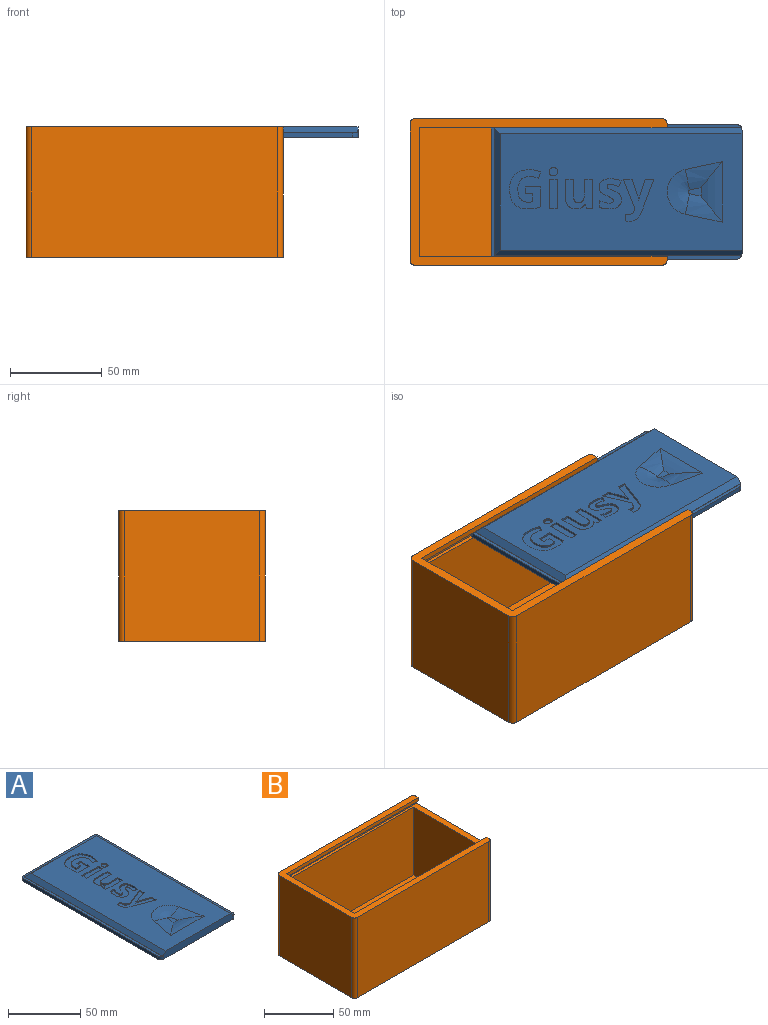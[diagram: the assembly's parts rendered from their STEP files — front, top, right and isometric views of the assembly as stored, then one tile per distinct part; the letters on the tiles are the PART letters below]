
ASSEMBLY  parts=2 mates=1
PART A: 116 faces, bbox 77.1x136.6x5.8 mm
  f0: plane 131.82x63.72mm, normal (0,0,1), area 6894.2mm2, adj f4,f10,f11,f12,f14,f15,f16,f17
  f1: plane 132.3x2.6mm, normal (1,0,0), area 344mm2, adj f5,f6,f112,f114
  f2: plane 70.7x2.6mm, normal (0,1,0), area 183.8mm2, adj f5,f6,f112,f113
  f3: plane 132.3x2.6mm, normal (-1,0,0), area 344mm2, adj f5,f6,f113,f115
  f4: plane 67.3x5.8mm, normal (0,-1,0), area 387.1mm2, adj f0,f6,f10,f11,f114,f115
  f5: plane 136.35x73.3mm, normal (0,0,1), area 612.8mm2, adj f1,f2,f3,f7,f8,f9,f112,f113
  f6: plane 136.6x73.3mm, normal (0,0,-1), area 10008.2mm2, adj f1,f2,f3,f4,f112,f113,f114,f115
  f7: plane 69.7x0.2mm, normal (0,1,0), area 13.9mm2, adj f5,f8,f9,f12
  f8: plane 134.55x0.2mm, normal (1,0,0), area 26.9mm2, adj f5,f7,f10,f114
  f9: plane 134.55x0.2mm, normal (-1,0,0), area 26.9mm2, adj f5,f7,f11,f115
  f10: plane 134.83x3.03mm, normal (0.71,0,0.71), area 565.4mm2, adj f0,f4,f8,f12,f114
  f11: plane 134.83x3.03mm, normal (-0.71,0,0.71), area 565.4mm2, adj f0,f4,f9,f12,f115
  f12: plane 69.7x3mm, normal (0,0.71,0.71), area 283mm2, adj f0,f7,f10,f11
  f13: plane 7.01x4.6mm, normal (0,0,1), area 21.5mm2, adj f14,f15,f16,f17
  f14: bspline ~22.47x15.51mm, area 157.5mm2, adj f0,f13,f15,f16
  f15: bspline ~24.43x12.28mm, area 213.3mm2, adj f0,f13,f14,f17
  f16: bspline ~57.85x11.49mm, area 220.1mm2, adj f0,f13,f14,f17
  f17: bspline ~22.47x15.51mm, area 157.5mm2, adj f0,f13,f15,f16
  f18: plane 15.81x6.33mm, normal (0.37,-0.93,0), area 17mm2, adj f0,f19,f34,f35
  f19: plane 1x0.78mm, normal (-0.31,-0.95,0), area 0.8mm2, adj f0,f18,f20,f35
  f20: extruded ~2.13x1.34mm, area 2.6mm2, adj f0,f19,f21,f35
  f21: extruded ~2.01x1mm, area 2.2mm2, adj f0,f20,f22,f35
  f22: extruded ~1.71x1mm, area 1.7mm2, adj f0,f21,f23,f35
  f23: plane 3.45x1mm, normal (0,-1,0), area 3.4mm2, adj f0,f22,f24,f35
  f24: extruded ~2.21x1mm, area 2.2mm2, adj f0,f23,f25,f35
  f25: extruded ~4.01x1.24mm, area 4.3mm2, adj f0,f24,f26,f35
  f26: extruded ~3.73x2.65mm, area 4.6mm2, adj f0,f25,f27,f35
  f27: plane 17.96x6.74mm, normal (0.35,0.94,0), area 19.2mm2, adj f0,f26,f28,f35
  f28: plane 4.66x1mm, normal (-1,0,0), area 4.7mm2, adj f0,f27,f29,f35
  f29: plane 8.96x2.95mm, normal (-0.31,-0.95,0), area 9.4mm2, adj f0,f28,f30,f35
  f30: extruded ~2.76x1mm, area 2.8mm2, adj f0,f29,f31,f35
  f31: plane 1x0.09mm, normal (-1,0,0), area 0.1mm2, adj f0,f30,f32,f35
  f32: extruded ~2.76x1mm, area 2.8mm2, adj f0,f31,f33,f35
  f33: plane 8.96x3mm, normal (-0.32,0.95,0), area 9.4mm2, adj f0,f32,f34,f35
  f34: plane 4.76x1mm, normal (-1,0,0), area 4.8mm2, adj f0,f18,f33,f35
  f35: plane 22.93x16.59mm, normal (0,0,1), area 165.6mm2, adj f18,f19,f20,f21,f22,f23,f24,f25
  f36: extruded ~2.04x1mm, area 2.1mm2, adj f0,f37,f61,f62
  f37: extruded ~1.51x1.28mm, area 2mm2, adj f0,f36,f38,f62
  f38: extruded ~2.73x1.41mm, area 3.1mm2, adj f0,f37,f39,f62
  f39: extruded ~2.72x1.27mm, area 3mm2, adj f0,f38,f40,f62
  f40: extruded ~1.01x1mm, area 1.2mm2, adj f0,f39,f41,f62
  f41: extruded ~1.92x1.04mm, area 2.4mm2, adj f0,f40,f42,f62
  f42: extruded ~2.12x1mm, area 2.2mm2, adj f0,f41,f43,f62
  f43: extruded ~2.24x1mm, area 2.4mm2, adj f0,f42,f44,f62
  f44: plane 3.13x1.31mm, normal (0.39,0.92,0), area 3.4mm2, adj f0,f43,f45,f62
  f45: extruded ~5.6x1.25mm, area 5.8mm2, adj f0,f44,f46,f62
  f46: extruded ~4.66x1.16mm, area 4.9mm2, adj f0,f45,f47,f62
  f47: extruded ~3.28x1.64mm, area 3.8mm2, adj f0,f46,f48,f62
  f48: extruded ~2.08x1mm, area 2.1mm2, adj f0,f47,f49,f62
  f49: extruded ~1.5x1.25mm, area 2mm2, adj f0,f48,f50,f62
  f50: extruded ~2.7x1.43mm, area 3.1mm2, adj f0,f49,f51,f62
  f51: extruded ~2.05x1mm, area 2.3mm2, adj f0,f50,f52,f62
  f52: extruded ~1.08x1mm, area 1.3mm2, adj f0,f51,f53,f62
  f53: extruded ~1x0.84mm, area 0.9mm2, adj f0,f52,f54,f62
  f54: extruded ~2.37x1.37mm, area 3.1mm2, adj f0,f53,f55,f62
  f55: extruded ~2.67x1mm, area 2.7mm2, adj f0,f54,f56,f62
  f56: extruded ~2.73x1mm, area 2.9mm2, adj f0,f55,f57,f62
  f57: plane 3.59x1mm, normal (0,-1,0), area 3.6mm2, adj f0,f56,f58,f62
  f58: extruded ~2.29x1mm, area 2.4mm2, adj f0,f57,f59,f62
  f59: extruded ~2.96x1mm, area 3mm2, adj f0,f58,f60,f62
  f60: extruded ~5.09x1.28mm, area 5.3mm2, adj f0,f59,f61,f62
  f61: extruded ~3.73x1.7mm, area 4.3mm2, adj f0,f36,f60,f62
  f62: plane 16.51x12.08mm, normal (0,0,1), area 127mm2, adj f36,f37,f38,f39,f40,f41,f42,f43
  f63: plane 3.33x1mm, normal (1,0,0), area 3.3mm2, adj f0,f64,f79,f80
  f64: plane 15.92x1mm, normal (0,1,0), area 15.9mm2, adj f0,f63,f65,f80
  f65: plane 4.34x1mm, normal (-1,0,0), area 4.3mm2, adj f0,f64,f66,f80
  f66: plane 7.49x1mm, normal (0,-1,0), area 7.5mm2, adj f0,f65,f67,f80
  f67: extruded ~4.04x1mm, area 4.2mm2, adj f0,f66,f68,f80
  f68: extruded ~2.63x1.22mm, area 3mm2, adj f0,f67,f69,f80
  f69: extruded ~1.95x1mm, area 2.2mm2, adj f0,f68,f70,f80
  f70: extruded ~2.58x1mm, area 2.7mm2, adj f0,f69,f71,f80
  f71: plane 9.3x1mm, normal (0,1,0), area 9.3mm2, adj f0,f70,f72,f80
  f72: plane 4.34x1mm, normal (-1,0,0), area 4.3mm2, adj f0,f71,f73,f80
  f73: plane 10.38x1mm, normal (0,-1,0), area 10.4mm2, adj f0,f72,f74,f80
  f74: extruded ~4.33x1.42mm, area 4.7mm2, adj f0,f73,f75,f80
  f75: extruded ~4.23x1.5mm, area 4.6mm2, adj f0,f74,f76,f80
  f76: extruded ~2.92x1mm, area 3mm2, adj f0,f75,f77,f80
  f77: extruded ~1.98x1.72mm, area 2.7mm2, adj f0,f76,f78,f80
  f78: plane 1x0.23mm, normal (1,0,0), area 0.2mm2, adj f0,f77,f79,f80
  f79: plane 2.04x1mm, normal (0.28,-0.96,0), area 2.1mm2, adj f0,f63,f78,f80
  f80: plane 16.21x14.7mm, normal (0,0,1), area 154.7mm2, adj f63,f64,f65,f66,f67,f68,f69,f70
  f81: plane 15.92x1mm, normal (0,1,0), area 15.9mm2, adj f0,f82,f84,f85
  f82: plane 4.34x1mm, normal (-1,0,0), area 4.3mm2, adj f0,f81,f83,f85
  f83: plane 15.92x1mm, normal (0,-1,0), area 15.9mm2, adj f0,f82,f84,f85
  f84: plane 4.34x1mm, normal (1,0,0), area 4.3mm2, adj f0,f81,f83,f85
  f85: plane 15.92x4.34mm, normal (0,0,1), area 69.2mm2, adj f81,f82,f83,f84
  f86: extruded ~2.37x2.14mm, area 3.7mm2, adj f0,f87,f90,f91
  f87: extruded ~1.78x1mm, area 1.9mm2, adj f0,f86,f88,f91
  f88: extruded ~1.57x1mm, area 1.7mm2, adj f0,f87,f89,f91
  f89: extruded ~2.37x2.12mm, area 3.6mm2, adj f0,f88,f90,f91
  f90: extruded ~2.37x2.12mm, area 3.6mm2, adj f0,f86,f89,f91
  f91: plane 4.73x4.26mm, normal (0,0,1), area 16.8mm2, adj f86,f87,f88,f89,f90
  f92: plane 3.68x1mm, normal (0,-1,0), area 3.7mm2, adj f0,f93,f110,f111
  f93: plane 3.95x1mm, normal (1,0,0), area 3.9mm2, adj f0,f92,f94,f111
  f94: plane 4.34x1mm, normal (0,-1,0), area 4.3mm2, adj f0,f93,f95,f111
  f95: extruded ~2.81x1mm, area 2.8mm2, adj f0,f94,f96,f111
  f96: extruded ~4.04x1.79mm, area 4.6mm2, adj f0,f95,f97,f111
  f97: extruded ~5.18x1.39mm, area 5.5mm2, adj f0,f96,f98,f111
  f98: extruded ~5.17x1.72mm, area 5.6mm2, adj f0,f97,f99,f111
  f99: extruded ~4.58x1.92mm, area 5.1mm2, adj f0,f98,f100,f111
  f100: extruded ~4.74x1.14mm, area 4.9mm2, adj f0,f99,f101,f111
  f101: plane 3.53x1.47mm, normal (0.38,0.92,0), area 3.8mm2, adj f0,f100,f102,f111
  f102: extruded ~6.18x1.28mm, area 6.4mm2, adj f0,f101,f103,f111
  f103: extruded ~7.99x2.82mm, area 8.7mm2, adj f0,f102,f104,f111
  f104: extruded ~7.86x2.88mm, area 8.6mm2, adj f0,f103,f105,f111
  f105: extruded ~7.96x2.49mm, area 8.5mm2, adj f0,f104,f106,f111
  f106: extruded ~7.2x2.77mm, area 8mm2, adj f0,f105,f107,f111
  f107: extruded ~3.62x1mm, area 3.6mm2, adj f0,f106,f108,f111
  f108: extruded ~3.78x1mm, area 3.9mm2, adj f0,f107,f109,f111
  f109: plane 10.8x1mm, normal (0,1,0), area 10.8mm2, adj f0,f108,f110,f111
  f110: plane 8.26x1mm, normal (-1,0,0), area 8.3mm2, adj f0,f92,f109,f111
  f111: plane 21.41x17.09mm, normal (0,0,1), area 211.2mm2, adj f92,f93,f94,f95,f96,f97,f98,f99
  f112: cylinder r=1.3mm len=2.6mm, axis (0,0,1), area 5.3mm2, adj f1,f2,f5,f6
  f113: cylinder r=1.3mm len=2.6mm, axis (0,0,-1), area 5.3mm2, adj f2,f3,f5,f6
  f114: cylinder r=3mm len=4mm, axis (0,0,-1), area 13.2mm2, adj f1,f4,f5,f6,f8,f10
  f115: cylinder r=3mm len=4mm, axis (0,0,1), area 13.2mm2, adj f3,f4,f5,f6,f9,f11
PART B: 27 faces, bbox 140x80x71 mm
  f0: plane 74x65mm, normal (1,0,0), area 4810mm2, adj f13,f15,f20,f23
  f1: plane 3x2mm, normal (1,0,0), area 6mm2, adj f2,f16,f23,f26
  f2: plane 135x3mm, normal (0,1,0), area 405mm2, adj f1,f3,f16,f26
  f3: plane 70x3mm, normal (1,0,0), area 210mm2, adj f2,f9,f16,f26
  f4: plane 130x60mm, normal (0,-1,0), area 7800mm2, adj f5,f11,f14,f15
  f5: plane 70x60mm, normal (-1,0,0), area 4200mm2, adj f4,f10,f14,f15
  f6: plane 3x2mm, normal (1,0,0), area 6mm2, adj f9,f16,f20,f26
  f7: plane 134x71mm, normal (0,1,0), area 9514mm2, adj f13,f20,f21,f26
  f8: plane 74x71mm, normal (-1,0,0), area 5254mm2, adj f13,f21,f22,f26
  f9: plane 135x3mm, normal (0,-1,0), area 405mm2, adj f3,f6,f16,f26
  f10: plane 130x60mm, normal (0,1,0), area 7800mm2, adj f5,f11,f14,f15
  f11: plane 70x60mm, normal (1,0,0), area 4200mm2, adj f4,f10,f14,f15
  f12: plane 134x71mm, normal (0,-1,0), area 9514mm2, adj f13,f22,f23,f26
  f13: plane 140x80mm, normal (0,0,-1), area 11192.3mm2, adj f0,f7,f8,f12,f20,f21,f22,f23
  f14: plane 130x70mm, normal (0,0,1), area 9100mm2, adj f4,f5,f10,f11
  f15: plane 137x74mm, normal (0,0,1), area 1037mm2, adj f0,f4,f5,f10,f11,f17,f18,f19
  f16: plane 137x74mm, normal (0,0,-1), area 687mm2, adj f1,f2,f3,f6,f9,f17,f18,f19
  f17: plane 135.5x3mm, normal (0,-1,0), area 406.5mm2, adj f15,f16,f20,f25
  f18: plane 71x3mm, normal (1,0,0), area 213mm2, adj f15,f16,f24,f25
  f19: plane 135.5x3mm, normal (0,1,0), area 406.5mm2, adj f15,f16,f23,f24
  f20: cylinder r=3mm len=71mm, axis (0,0,-1), area 334.6mm2, adj f0,f6,f7,f13,f17,f26
  f21: cylinder r=3mm len=71mm, axis (0,0,1), area 334.6mm2, adj f7,f8,f13,f26
  f22: cylinder r=3mm len=71mm, axis (0,0,-1), area 334.6mm2, adj f8,f12,f13,f26
  f23: cylinder r=3mm len=71mm, axis (0,0,1), area 334.6mm2, adj f0,f1,f12,f13,f19,f26
  f24: cylinder r=1.5mm len=3mm, axis (0,0,1), area 7.1mm2, adj f15,f16,f18,f19
  f25: cylinder r=1.5mm len=3mm, axis (0,0,1), area 7.1mm2, adj f15,f16,f17,f18
  f26: plane 140x80mm, normal (0,0,1), area 1742.3mm2, adj f1,f2,f3,f6,f7,f8,f9,f12
PLACE A rot(axis=(0,0,1),90deg) t=(20.52,-0.65,76.72)mm
PLACE B t=(-22,-0.65,11.52)mm fixed
MATE slider A.f2 <-> B.f18  axis (-1,0,0) through (-47.78,-0.65,78.02)mm
